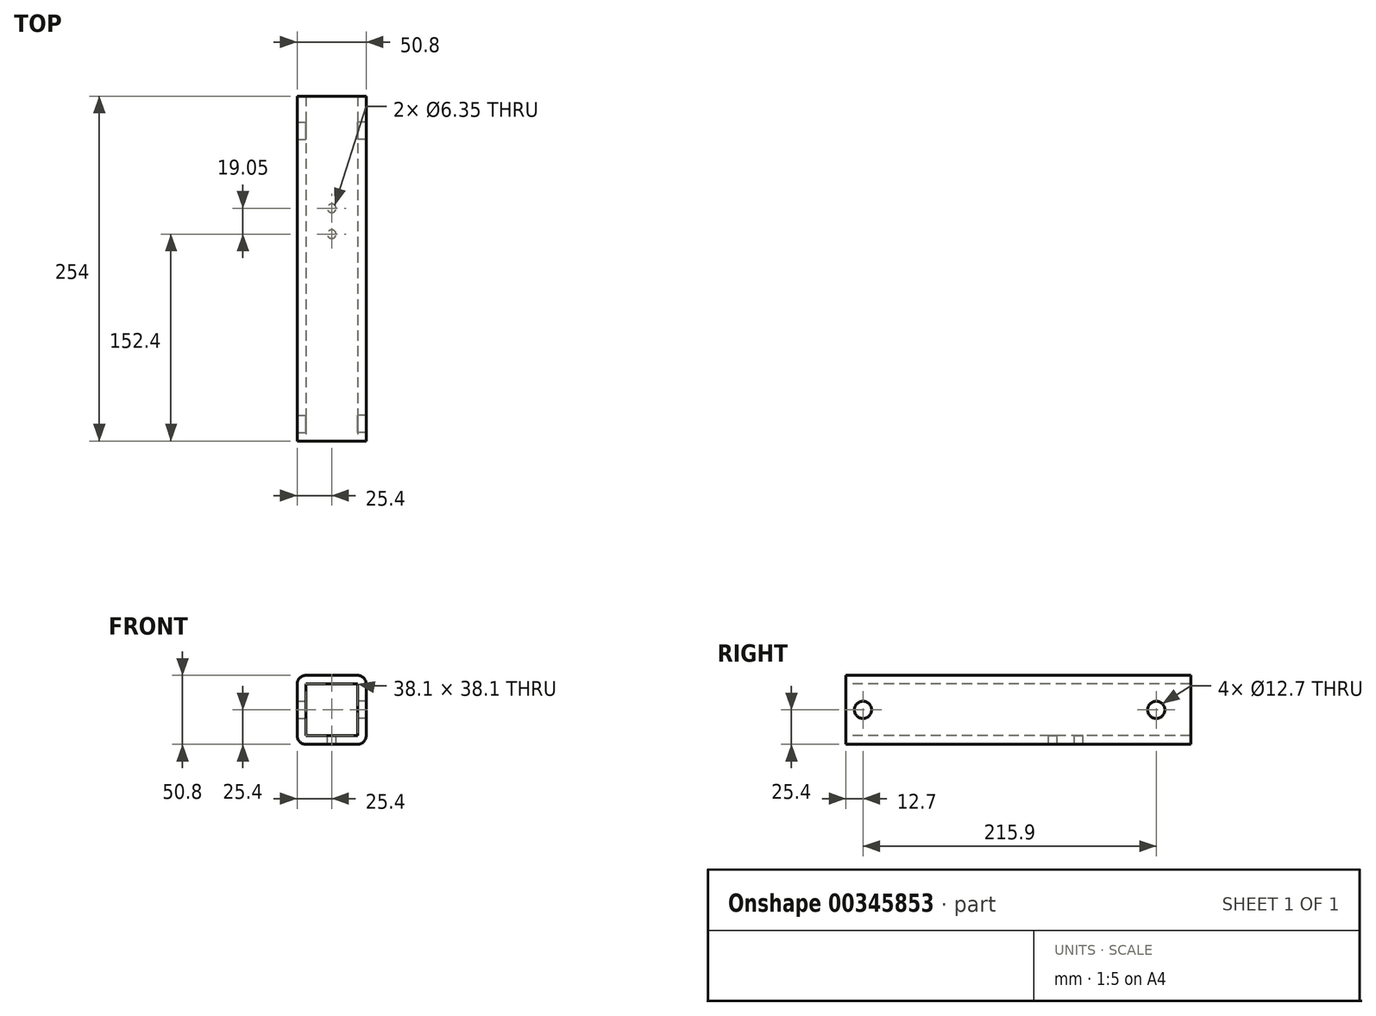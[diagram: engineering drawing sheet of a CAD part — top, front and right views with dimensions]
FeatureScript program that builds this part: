
annotation { "Feature Type Name" : "Feature", "Feature Type Description" : "" }
export const myFeature = defineFeature(function(context is Context, id is Id, definition is map)
    precondition{}
    {
        {
            var Q0;
            Q0=qCreatedBy(makeId("Front.planeOp"),FACE);
            var sketch = newSketch(context, id + "F0", { "sketchPlane" : qUnion([Q0])});
            skLineSegment(sketch, "E0.bottom", {"start": v(19.05, -25.4) * mm, "end": v(-19.05, -25.4) * mm});
            skLineSegment(sketch, "E0.top", {"start": v(19.05, 25.4) * mm, "end": v(-19.05, 25.4) * mm});
            skLineSegment(sketch, "E0.left", {"start": v(25.4, -19.05) * mm, "end": v(25.4, 19.05) * mm});
            skLineSegment(sketch, "E0.right", {"start": v(-25.4, -19.05) * mm, "end": v(-25.4, 19.05) * mm});
            skPoint(sketch, "E0.middle", {"position": v(0, 0) * mm});
            skPoint(sketch, "E1.visualSharp", {"position": v(-25.4, 25.4) * mm});
            skArc(sketch, "E1.filletArc", {"start": v(-19.05, 25.4) * mm, "mid": v(-23.54, 23.54) * mm, "end": v(-25.4, 19.05) * mm});
            skPoint(sketch, "E2.visualSharp", {"position": v(25.4, 25.4) * mm});
            skArc(sketch, "E2.filletArc", {"start": v(25.4, 19.05) * mm, "mid": v(23.54, 23.54) * mm, "end": v(19.05, 25.4) * mm});
            skPoint(sketch, "E3.visualSharp", {"position": v(25.4, -25.4) * mm});
            skArc(sketch, "E3.filletArc", {"start": v(19.05, -25.4) * mm, "mid": v(23.54, -23.54) * mm, "end": v(25.4, -19.05) * mm});
            skPoint(sketch, "E4.visualSharp", {"position": v(-25.4, -25.4) * mm});
            skArc(sketch, "E4.filletArc", {"start": v(-25.4, -19.05) * mm, "mid": v(-23.54, -23.54) * mm, "end": v(-19.05, -25.4) * mm});
            skLineSegment(sketch, "E5.bottom", {"start": v(19.05, -19.05) * mm, "end": v(-19.05, -19.05) * mm});
            skLineSegment(sketch, "E5.top", {"start": v(19.05, 19.05) * mm, "end": v(-19.05, 19.05) * mm});
            skLineSegment(sketch, "E5.left", {"start": v(19.05, -19.05) * mm, "end": v(19.05, 19.05) * mm});
            skLineSegment(sketch, "E5.right", {"start": v(-19.05, -19.05) * mm, "end": v(-19.05, 19.05) * mm});
            skSolve(sketch);
        }
        {
            var Q0;
            Q0=makeQuery(id+"F0.imprint","IMPRINT",FACE,{"disambiguationData":[TD([[makeQuery(id+"F0.imprint","IMPRINT",EDGE,{"derivedFrom":sQuery(id+"F0.wireOp",EDGE,"E0.bottom")}),-1.0]])]});
            extrude(context, id + "F4", {"entities" : qUnion([Q0]), "oppositeDirection" : true, "depth" : 254 * mm});
        }
        {
            var Q0;
            Q0=qCreatedBy(makeId("Right.planeOp"),FACE);
            var sketch = newSketch(context, id + "F5", { "sketchPlane" : qUnion([Q0])});
            skPoint(sketch, "E6", {"position": v(12.7, 0) * mm});
            skPoint(sketch, "E7", {"position": v(50.8, 0) * mm});
            skPoint(sketch, "E8", {"position": v(88.9, 0) * mm});
            skPoint(sketch, "E9", {"position": v(127, 0) * mm});
            skPoint(sketch, "E10", {"position": v(228.6, 0) * mm});
            skSolve(sketch);
        }
        {
            var Q0;
            Q0=sQuery(id+"F5.wireOp",VERTEX,"E6");
            var Q1;
            Q1=sQuery(id+"F5.wireOp",VERTEX,"E10");
            var Q2;
            Q2=makeQuery(id+"F4.opExtrude","SWEPT_BODY",BODY,{"disambiguationData":[OSD([sQuery(id+"F0.wireOp",EDGE,"E0.bottom"),sQuery(id+"F0.wireOp",EDGE,"E0.top"),sQuery(id+"F0.wireOp",EDGE,"E0.left"),sQuery(id+"F0.wireOp",EDGE,"E0.right"),sQuery(id+"F0.wireOp",EDGE,"E1.filletArc"),sQuery(id+"F0.wireOp",EDGE,"E2.filletArc"),sQuery(id+"F0.wireOp",EDGE,"E3.filletArc"),sQuery(id+"F0.wireOp",EDGE,"E4.filletArc"),sQuery(id+"F0.wireOp",EDGE,"E5.bottom"),sQuery(id+"F0.wireOp",EDGE,"E5.top"),sQuery(id+"F0.wireOp",EDGE,"E5.left"),sQuery(id+"F0.wireOp",EDGE,"E5.right")])]});
            hole(context, id + "F6", {"style" : HoleStyle.SIMPLE, "endStyle" : HoleEndStyle.THROUGH, "oppositeDirection" : true, "holeDiameter" : 12.7 * mm, "locations" : qUnion([Q0, Q1]), "scope" : qUnion([Q2]), "isTappedThrough" : true});
        }
        {
            var Q0;
            Q0=sQuery(id+"F5.wireOp",VERTEX,"E6");
            var Q1;
            Q1=sQuery(id+"F5.wireOp",VERTEX,"E10");
            var Q2;
            Q2=makeQuery(id+"F4.opExtrude","SWEPT_BODY",BODY,{"disambiguationData":[OSD([sQuery(id+"F0.wireOp",EDGE,"E0.bottom"),sQuery(id+"F0.wireOp",EDGE,"E0.top"),sQuery(id+"F0.wireOp",EDGE,"E0.left"),sQuery(id+"F0.wireOp",EDGE,"E0.right"),sQuery(id+"F0.wireOp",EDGE,"E1.filletArc"),sQuery(id+"F0.wireOp",EDGE,"E2.filletArc"),sQuery(id+"F0.wireOp",EDGE,"E3.filletArc"),sQuery(id+"F0.wireOp",EDGE,"E4.filletArc"),sQuery(id+"F0.wireOp",EDGE,"E5.bottom"),sQuery(id+"F0.wireOp",EDGE,"E5.top"),sQuery(id+"F0.wireOp",EDGE,"E5.left"),sQuery(id+"F0.wireOp",EDGE,"E5.right")])]});
            hole(context, id + "F1", {"style" : HoleStyle.SIMPLE, "endStyle" : HoleEndStyle.THROUGH, "holeDiameter" : 12.7 * mm, "locations" : qUnion([Q0, Q1]), "scope" : qUnion([Q2]), "isTappedThrough" : true});
        }
        {
            var Q0;
            Q0=qCreatedBy(makeId("Top.planeOp"),FACE);
            var sketch = newSketch(context, id + "F2", { "sketchPlane" : qUnion([Q0])});
            skPoint(sketch, "E11", {"position": v(0, 171.45) * mm});
            skPoint(sketch, "E12", {"position": v(0, 152.4) * mm});
            skSolve(sketch);
        }
        {
            var Q0;
            Q0=sQuery(id+"F2.wireOp",VERTEX,"E11");
            var Q1;
            Q1=sQuery(id+"F2.wireOp",VERTEX,"E12");
            var Q2;
            Q2=makeQuery(id+"F4.opExtrude","SWEPT_BODY",BODY,{"disambiguationData":[OSD([sQuery(id+"F0.wireOp",EDGE,"E0.bottom"),sQuery(id+"F0.wireOp",EDGE,"E0.top"),sQuery(id+"F0.wireOp",EDGE,"E0.left"),sQuery(id+"F0.wireOp",EDGE,"E0.right"),sQuery(id+"F0.wireOp",EDGE,"E1.filletArc"),sQuery(id+"F0.wireOp",EDGE,"E2.filletArc"),sQuery(id+"F0.wireOp",EDGE,"E3.filletArc"),sQuery(id+"F0.wireOp",EDGE,"E4.filletArc"),sQuery(id+"F0.wireOp",EDGE,"E5.bottom"),sQuery(id+"F0.wireOp",EDGE,"E5.top"),sQuery(id+"F0.wireOp",EDGE,"E5.left"),sQuery(id+"F0.wireOp",EDGE,"E5.right")])]});
            hole(context, id + "F3", {"style" : HoleStyle.SIMPLE, "endStyle" : HoleEndStyle.THROUGH, "holeDiameter" : 6.35 * mm, "locations" : qUnion([Q0, Q1]), "scope" : qUnion([Q2]), "isTappedThrough" : true});
        }
    });
